# Revit family: VTp701 Соединитель с переходом на НР
name_source: partatom
category: Соединительные детали трубопроводов
revit_build: Autodesk Revit 2015 (Build: 20140606_1530(x64)
units: mm (PartAtom-declared; Revit-internal decimal feet)

## types (7) — shared parameters
Группа модели = VTp.700
Изготовитель = VALTEC S.R.L.
Коэффициент K = 0.5

## per-type parameters (varying)
| type | 20х1/2" | 20х3/4" | 25х1/2" | 25х3/4" | 32х1" | 32х1/2" | 32х3/4" | A | B | C | G | d | Код по классификатору | Описание |
| 20х1/2" | Да | Нет | Нет | Нет | Нет | Нет | Нет | 50 мм | 13 мм | 15 мм | 15 мм | 20 мм | VTp.701.0.02004 | Соединитель с переходом на наружн. резьбу |
| 20х3/4" | Нет | Да | Нет | Нет | Нет | Нет | Нет | 50 мм | 14 мм | 15 мм | 20 мм | 20 мм | VTp.701.0.02005 | Соединитель с переходом на внутр. резьбу |
| 25х1/2" | Нет | Нет | Да | Нет | Нет | Нет | Нет | 53 мм | 13 мм | 17 мм | 15 мм | 25 мм | VTp.701.0.02504 | Соединитель с переходом на наружн. резьбу |
| 25х3/4" | Нет | Нет | Нет | Да | Нет | Нет | Нет | 54 мм | 14 мм | 17 мм | 20 мм | 25 мм | VTp.701.0.02505 | Соединитель с переходом на наружн. резьбу |
| 32х1/2" | Нет | Нет | Нет | Нет | Нет | Да | Нет | 53 мм | 13 мм | 19 мм | 15 мм | 32 мм | VTp.701.0.03204 | Соединитель с переходом на наружн. резьбу |
| 32х3/4" | Нет | Нет | Нет | Нет | Нет | Нет | Да | 56 мм | 14 мм | 20 мм | 20 мм | 32 мм | VTp.701.0.03205 | Соединитель с переходом на наружн. резьбу |
| 32х1" | Нет | Нет | Нет | Нет | Да | Нет | Нет | 58 мм | 14 мм | 21 мм | 25 мм | 32 мм | VTp.701.0.03206 | Соединитель с переходом на наружн. реззьбу |
